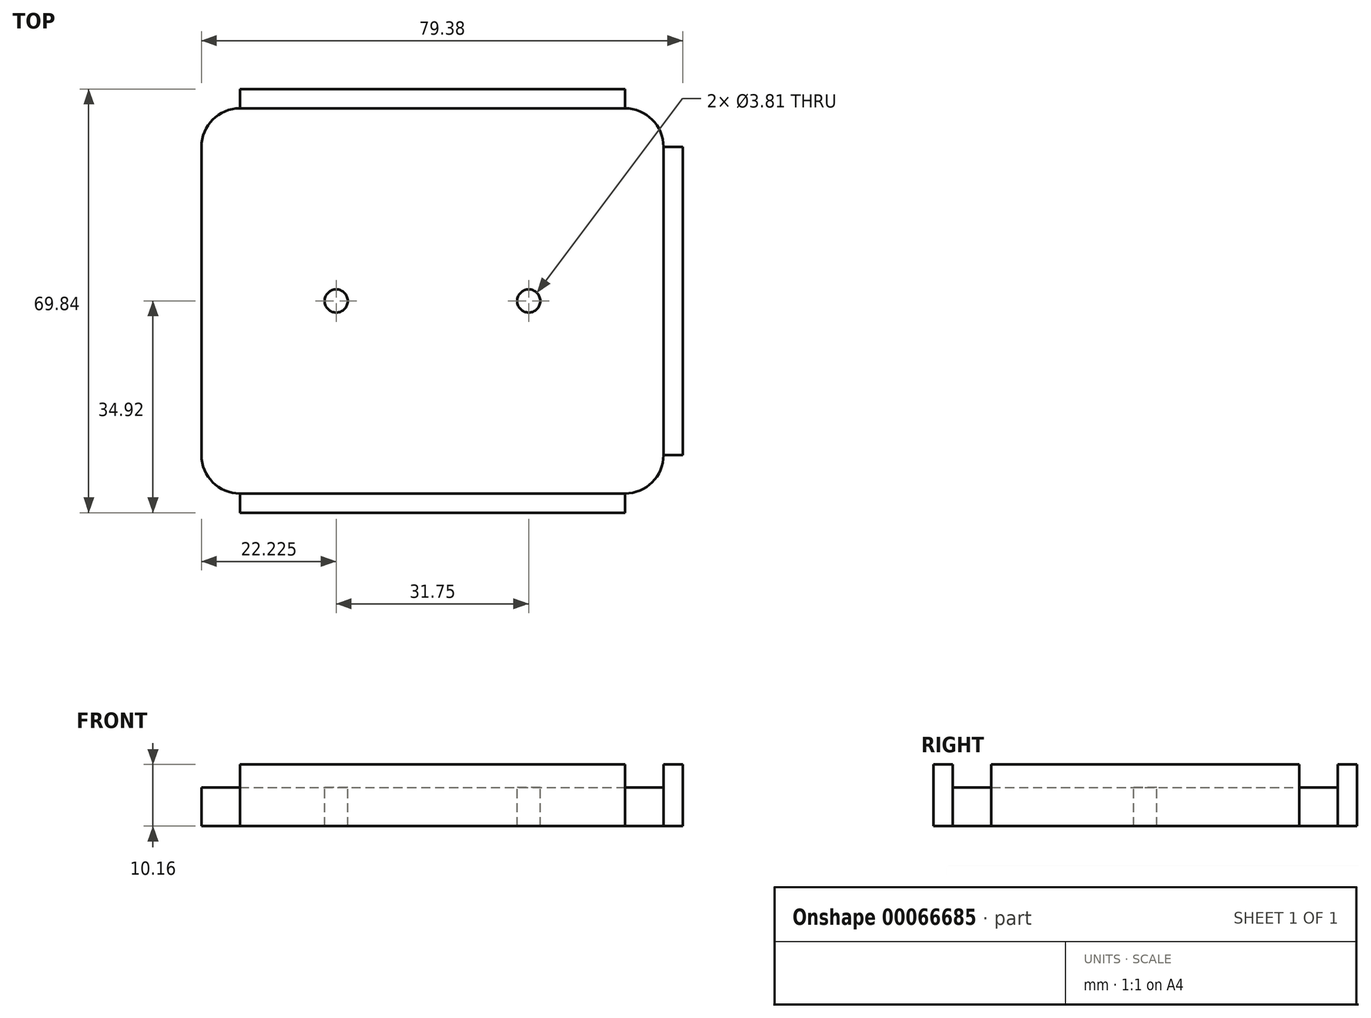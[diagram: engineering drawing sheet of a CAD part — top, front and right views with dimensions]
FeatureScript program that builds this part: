
annotation { "Feature Type Name" : "Feature", "Feature Type Description" : "" }
export const myFeature = defineFeature(function(context is Context, id is Id, definition is map)
    precondition{}
    {
        {
            var Q0;
            Q0=qCreatedBy(makeId("Top.planeOp"),FACE);
            var sketch = newSketch(context, id + "F0", { "sketchPlane" : qUnion([Q0])});
            skLineSegment(sketch, "E0.bottom", {"start": v(6.35, 0) * mm, "end": v(69.85, 0) * mm});
            skLineSegment(sketch, "E0.top", {"start": v(6.35, 63.5) * mm, "end": v(69.85, 63.5) * mm});
            skLineSegment(sketch, "E0.left", {"start": v(0, 6.35) * mm, "end": v(0, 57.15) * mm});
            skLineSegment(sketch, "E0.right", {"start": v(76.2, 6.35) * mm, "end": v(76.2, 57.15) * mm});
            skPoint(sketch, "E1.visualSharp", {"position": v(0, 63.5) * mm});
            skArc(sketch, "E1.filletArc", {"start": v(6.35, 63.5) * mm, "mid": v(1.86, 61.64) * mm, "end": v(0, 57.15) * mm});
            skPoint(sketch, "E2.visualSharp", {"position": v(0, 0) * mm});
            skArc(sketch, "E2.filletArc", {"start": v(0, 6.35) * mm, "mid": v(1.86, 1.86) * mm, "end": v(6.35, 0) * mm});
            skPoint(sketch, "E3.visualSharp", {"position": v(76.2, 0) * mm});
            skArc(sketch, "E3.filletArc", {"start": v(69.85, 0) * mm, "mid": v(74.34, 1.86) * mm, "end": v(76.2, 6.35) * mm});
            skPoint(sketch, "E4.visualSharp", {"position": v(76.2, 63.5) * mm});
            skArc(sketch, "E4.filletArc", {"start": v(76.2, 57.15) * mm, "mid": v(74.34, 61.64) * mm, "end": v(69.85, 63.5) * mm});
            skSolve(sketch);
        }
        {
            var Q0;
            Q0=makeQuery(id+"F0.imprint","IMPRINT",FACE,{"disambiguationData":[TD([[makeQuery(id+"F0.imprint","IMPRINT",EDGE,{"derivedFrom":sQuery(id+"F0.wireOp",EDGE,"E0.bottom")}),1.0]])]});
            extrude(context, id + "F1", {"entities" : qUnion([Q0]), "depth" : 6.35 * mm});
        }
        {
            var Q0;
            Q0=makeQuery(id+"F1.opExtrude","CAP_FACE",FACE,{"disambiguationData":[OSD([sQuery(id+"F0.wireOp",EDGE,"E0.bottom"),sQuery(id+"F0.wireOp",EDGE,"E0.top"),sQuery(id+"F0.wireOp",EDGE,"E0.left"),sQuery(id+"F0.wireOp",EDGE,"E0.right"),sQuery(id+"F0.wireOp",EDGE,"E1.filletArc"),sQuery(id+"F0.wireOp",EDGE,"E2.filletArc"),sQuery(id+"F0.wireOp",EDGE,"E3.filletArc"),sQuery(id+"F0.wireOp",EDGE,"E4.filletArc")])],"isStart":false});
            var sketch = newSketch(context, id + "F2", { "sketchPlane" : qUnion([Q0])});
            skLineSegment(sketch, "E5", {"start": v(0, 31.75) * mm, "end": v(22.23, 31.75) * mm});
            skLineSegment(sketch, "E6", {"start": v(22.23, 31.75) * mm, "end": v(53.98, 31.75) * mm});
            skLineSegment(sketch, "E7", {"start": v(53.98, 31.75) * mm, "end": v(76.2, 31.75) * mm});
            skCircle(sketch, "E8", {"center": v(22.23, 31.75) * mm, "radius": 1.9 * mm});
            skCircle(sketch, "E9", {"center": v(53.98, 31.75) * mm, "radius": 1.9 * mm});
            skSolve(sketch);
        }
        {
            var Q0;
            Q0 = qSketchRegion(id + "F2", true);
            extrude(context, id + "F3", {"entities" : qUnion([Q0]), "operationType" : NewBodyOperationType.REMOVE, "endBound" : BoundingType.THROUGH_ALL, "oppositeDirection" : true, "depth" : 25.4 * mm});
        }
        {
            var Q0;
            Q0=makeQuery(id+"F1.opExtrude","CAP_FACE",FACE,{"disambiguationData":[OSD([sQuery(id+"F0.wireOp",EDGE,"E0.bottom"),sQuery(id+"F0.wireOp",EDGE,"E0.top"),sQuery(id+"F0.wireOp",EDGE,"E0.left"),sQuery(id+"F0.wireOp",EDGE,"E0.right"),sQuery(id+"F0.wireOp",EDGE,"E1.filletArc"),sQuery(id+"F0.wireOp",EDGE,"E2.filletArc"),sQuery(id+"F0.wireOp",EDGE,"E3.filletArc"),sQuery(id+"F0.wireOp",EDGE,"E4.filletArc")])],"isStart":true});
            var sketch = newSketch(context, id + "F4", { "sketchPlane" : qUnion([Q0])});
            skLineSegment(sketch, "E10.bottom", {"start": v(6.35, 0) * mm, "end": v(69.85, 0) * mm});
            skLineSegment(sketch, "E10.top", {"start": v(6.35, 3.17) * mm, "end": v(69.85, 3.17) * mm});
            skLineSegment(sketch, "E10.left", {"start": v(6.35, 0) * mm, "end": v(6.35, 3.17) * mm});
            skLineSegment(sketch, "E10.right", {"start": v(69.85, 0) * mm, "end": v(69.85, 3.17) * mm});
            skLineSegment(sketch, "E11.bottom", {"start": v(76.2, -6.35) * mm, "end": v(79.38, -6.35) * mm});
            skLineSegment(sketch, "E11.top", {"start": v(76.2, -57.15) * mm, "end": v(79.38, -57.15) * mm});
            skLineSegment(sketch, "E11.left", {"start": v(76.2, -6.35) * mm, "end": v(76.2, -57.15) * mm});
            skLineSegment(sketch, "E11.right", {"start": v(79.38, -6.35) * mm, "end": v(79.38, -57.15) * mm});
            skLineSegment(sketch, "E12.bottom", {"start": v(69.85, -63.5) * mm, "end": v(6.35, -63.5) * mm});
            skLineSegment(sketch, "E12.top", {"start": v(69.85, -66.67) * mm, "end": v(6.35, -66.67) * mm});
            skLineSegment(sketch, "E12.left", {"start": v(69.85, -63.5) * mm, "end": v(69.85, -66.67) * mm});
            skLineSegment(sketch, "E12.right", {"start": v(6.35, -63.5) * mm, "end": v(6.35, -66.67) * mm});
            skSolve(sketch);
        }
        {
            var Q0;
            Q0 = qSketchRegion(id + "F4", true);
            extrude(context, id + "F5", {"entities" : qUnion([Q0]), "operationType" : NewBodyOperationType.ADD, "oppositeDirection" : true, "depth" : 10.16 * mm});
        }
    });
